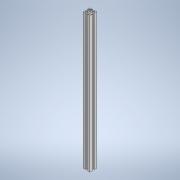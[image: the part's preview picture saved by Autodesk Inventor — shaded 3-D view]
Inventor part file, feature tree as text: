
AUTODESK INVENTOR PART (.ipt)
format: ipt  version: 2022 (Build 260153000, 153)  size: 154,112 bytes
history: native  units: in
note: dims shown in document units (in); Inventor stores cm internally (conversion verified against a paired STEP export)
features: sketch x2, extrude x1, hole x1
ambient origin geometry x8: Origin, YZ Plane, XZ Plane, XY Plane, X Axis, Y Axis, Z Axis, Center Point
bodies: Body1 (feature_tree)
feature tree (4):
  extrude  "Extrusion1"  [1 undecoded]
  hole  "Hole1"  [1 undecoded]
  sketch  "Sketch1"  dims[d0=15.748in d1=0.0in]
  sketch  "Sketch2"  dims[d2=0.1575in d3=0.2362in d4=0.1575in d5=0.0787in d6=90.0deg d7=0.315in d8=0.8108in]
note: 2 required parameter values undecoded (feature->parameter linkage not recoverable at this tier; creation-order binding heuristic only, values carry confidence <= 0.55)
